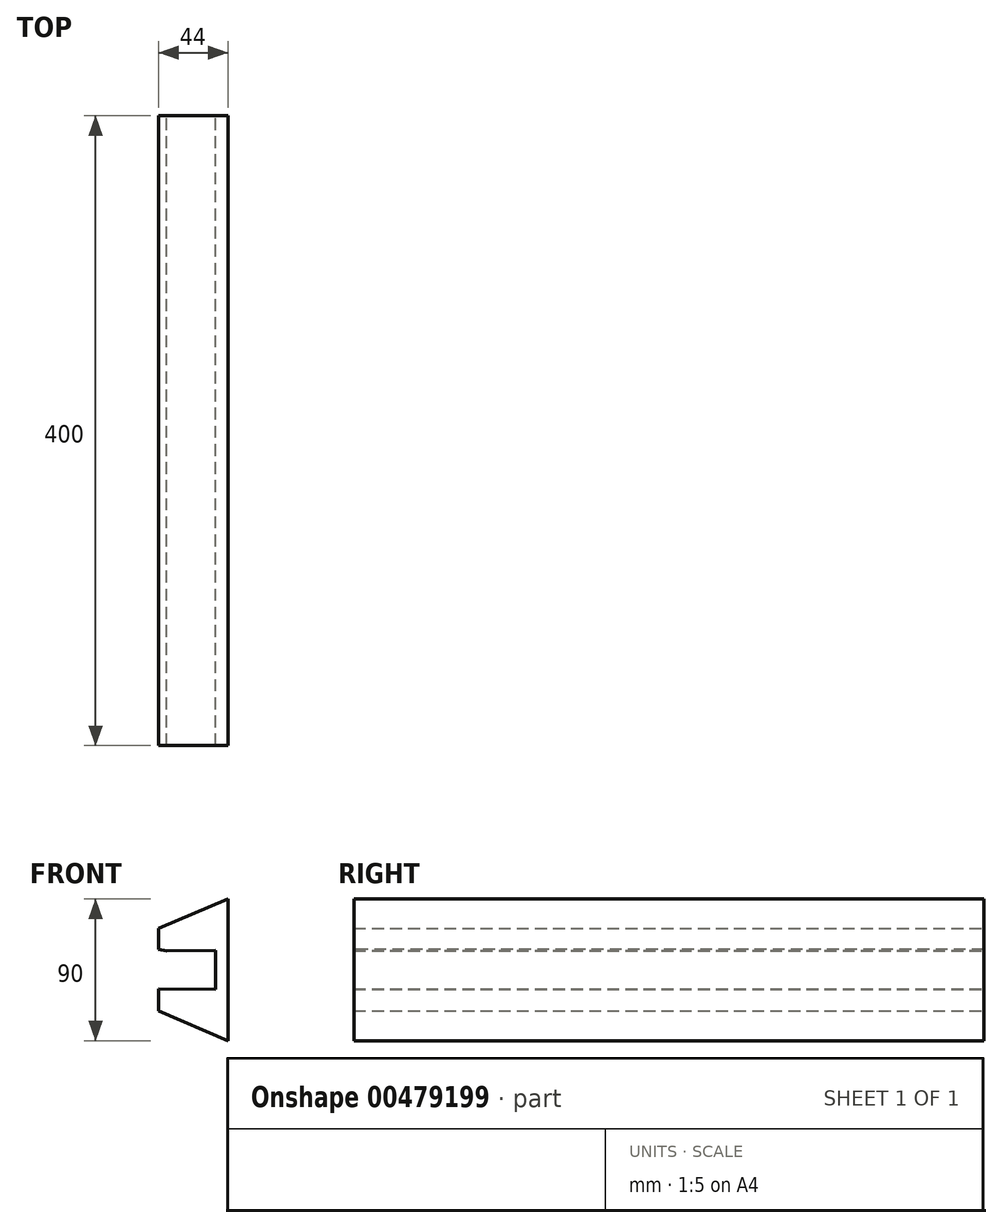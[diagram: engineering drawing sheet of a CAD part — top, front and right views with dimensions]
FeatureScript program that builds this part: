
annotation { "Feature Type Name" : "Feature", "Feature Type Description" : "" }
export const myFeature = defineFeature(function(context is Context, id is Id, definition is map)
    precondition{}
    {
        {
            var Q0;
            Q0=qCreatedBy(makeId("Front.planeOp"),FACE);
            var sketch = newSketch(context, id + "F0", { "sketchPlane" : qUnion([Q0])});
            skLineSegment(sketch, "E0", {"start": v(-25.94, 5.62) * mm, "end": v(-25.94, -18.28) * mm});
            skLineSegment(sketch, "E1", {"start": v(10.06, 6.12) * mm, "end": v(10.06, -18.78) * mm});
            skPoint(sketch, "E2", {"position": v(-25.94, -6.33) * mm});
            skPoint(sketch, "E3", {"position": v(10.06, -6.33) * mm});
            skLineSegment(sketch, "E4", {"start": v(-25.94, 5.62) * mm, "end": v(10.06, 6.12) * mm});
            skLineSegment(sketch, "E5", {"start": v(-25.94, -18.28) * mm, "end": v(10.06, -18.78) * mm});
            skLineSegment(sketch, "E6", {"start": v(-25.94, 5.62) * mm, "end": v(-25.94, 19.87) * mm});
            skLineSegment(sketch, "E7", {"start": v(-25.94, 19.87) * mm, "end": v(18.06, 38.67) * mm});
            skLineSegment(sketch, "E8", {"start": v(18.06, 38.67) * mm, "end": v(18.06, -6.33) * mm});
            skLineSegment(sketch, "E9", {"start": v(-25.94, -6.33) * mm, "end": v(10.06, -6.33) * mm, "construction": true});
            skLineSegment(sketch, "E10.MirrorCS", {"start": v(-25.94, -18.28) * mm, "end": v(-25.94, -32.53) * mm});
            skLineSegment(sketch, "E11.MirrorCS", {"start": v(-25.94, -32.53) * mm, "end": v(18.06, -51.33) * mm});
            skLineSegment(sketch, "E12.MirrorCS", {"start": v(18.06, -51.33) * mm, "end": v(18.06, -6.33) * mm});
            skSolve(sketch);
        }
        {
            var Q0;
            Q0=makeQuery(id+"F0.imprint","IMPRINT",FACE,{"disambiguationData":[TD([[makeQuery(id+"F0.imprint","IMPRINT",EDGE,{"derivedFrom":sQuery(id+"F0.wireOp",EDGE,"E1")}),1.0]])]});
            extrude(context, id + "F1", {"entities" : qUnion([Q0]), "depth" : 400 * mm});
        }
        {
            var Q0;
            Q0=makeQuery(id+"F1.opExtrude","SWEPT_EDGE",EDGE,{"disambiguationData":[OSD([sQuery(id+"F0.wireOp",EDGE,"E0"),sQuery(id+"F0.wireOp",EDGE,"E4"),sQuery(id+"F0.wireOp",EDGE,"E6")])]});
            chamfer(context, id + "F2", {"entities" : qUnion([Q0]), "chamferType" : ChamferType.TWO_OFFSETS, "width1" : 5 * mm, "oppositeDirection" : false, "width2" : 1 * mm, "tangentPropagation" : true});
        }
    });
